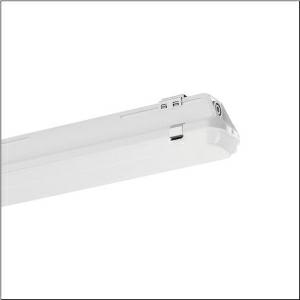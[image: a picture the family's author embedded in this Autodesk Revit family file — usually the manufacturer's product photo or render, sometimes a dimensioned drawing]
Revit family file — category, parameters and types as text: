
# Revit family: monsun_r__21_51fb30mp480b_19bf
name_source: partatom
category: Lighting Fixtures
units: mm (PartAtom-declared; Revit-internal decimal feet)

## family parameters
Cut with Voids When Loaded = No
Host = Face
Light Source = No
Part Type = Normal
Room Calculation Point = No
Round Connector Dimension = Use Diameter
Shared = No

## types (1)
- --- (1 x LED, 7750 lm, 53.6 W, 4000K)
    Apparent Load = 54 VA
    CIE Flux Codes = 48 77 93 95 100
    Color Rendering = 80
    Color Temperature = 4000K
    Default Elevation = 1800 mm
    Description = Monsun® 21, damp-proof luminaire, chain hanger, primary optical cover: enclosure, of PA, light emission: direct distribution, primary light characteristic: symmetric, installation type: suspended mounting, surface-mounted, horizontal mounting, vertical mounting, LED, rated luminous flux: 7.750lm, luminous efficacy: 145lm/W, light colour: 840, colour temperature: 4000K, control gear: ECG, with terminal, 3-pole, max. 2.5mm², mains connection: 220..240V, AC, 50/60Hz, rated input power: 54W, housing, of glass-fibre reinforced polyester, uncoated, bright grey, length: 1.590mm, width: 90mm, height: 88mm, clip for enclosure, of stainless steel (V2A), ceiling mounting element, of stainless steel (V2A), chain hanger, of stainless steel (V2A), protection rating (complete): IP66, insulation class (complete): insulation class I (protective earthing), certification: CE, ENEC, VDE, UKCA, protection symbol: D, impact resistance: IK08, permissible operating ambient temperature: -25..+35°C, standard: EN 50419, EN 60598-2-1, corresponds to IFS (International Featured Standards) requirements for safety and quality in the food industry, for indoor or canopied outdoor use, no direct snow, no direct sun, no direct rain, packaging unit: 1 piece
    Height = 89 mm
    Lamp = 1 x LED
    Lamp Light Flux = 7750 lm
    Lamp Power = 53.6 W
    Lamp count = 1
    Length = 1590 mm
    Luminous efficacy = 145 lm/W
    Manufacturer = Siteco
    ModVariant = No
    Model = 51FB30MP480B
    Mounting Place = Ceiling
    Mounting Type = Pendant
    Number of Poles = 1
    OnlyDefault = Yes
    Power Factor = 1
    Product Name = Monsun® 21
    Product group = damp-proof luminaire | ceiling pendant
    ProductGroupID = 908
    Protection Class = Protection class I
    Protection Degree = IP 66
    RLX_Detail_Level = 1
    RlxData = <blob elided: 89589 chars, md5=94497a86>
    Socket = socket
    Standby Power = 0 W
    System Light Flux = 7750 lm
    System Power = 54 W
    Type Comments = factory setting: luminous flux: 100 % | (A | C | E) | 121 mA
    Type Image = l_1006717.jpg
    URL = http://relux.com
    VarID = @adj_056883
    Voltage = 0 V
    Weight = 0.00 kg
    Width = 90 mm

## geometry (parser evidence)
native form markers: Blend x4, Sweep x14
no freeform markers — native parametric forms only
